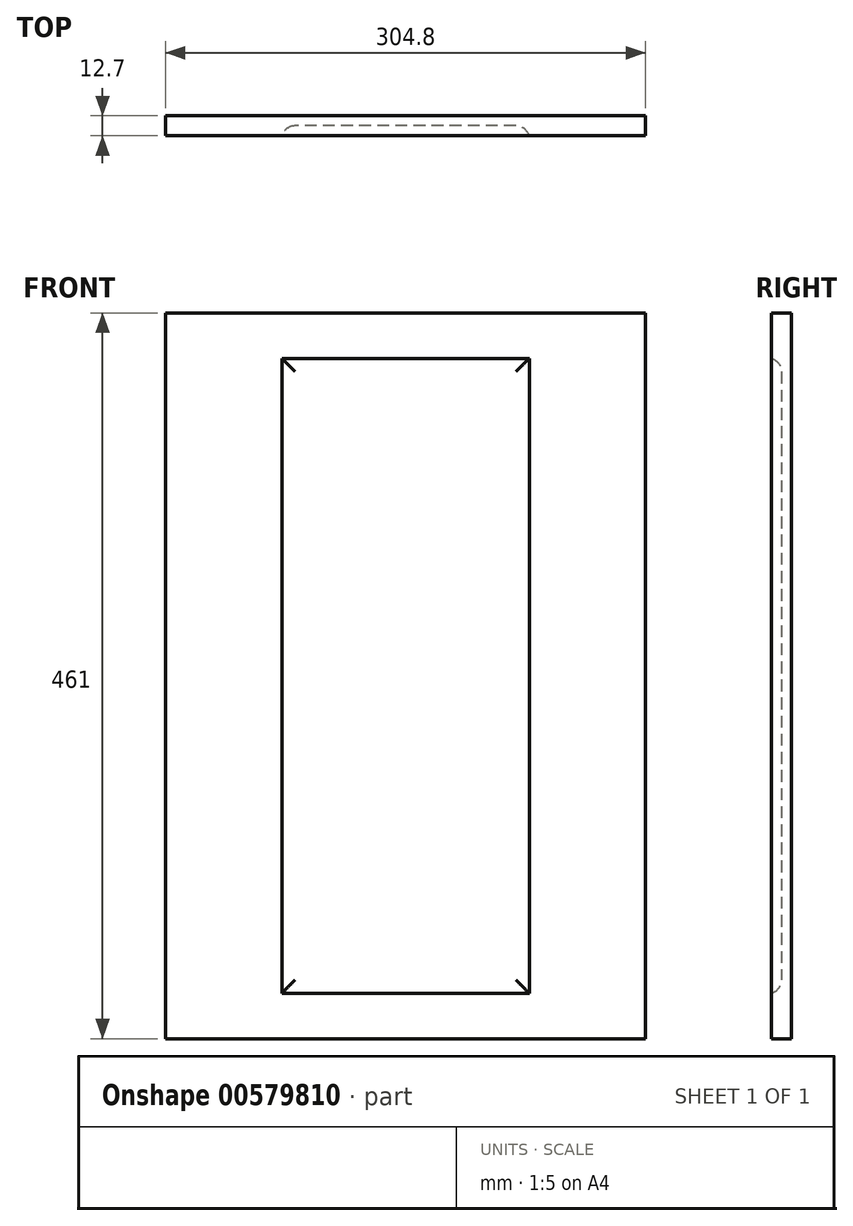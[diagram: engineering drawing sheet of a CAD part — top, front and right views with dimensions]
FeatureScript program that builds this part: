
annotation { "Feature Type Name" : "Feature", "Feature Type Description" : "" }
export const myFeature = defineFeature(function(context is Context, id is Id, definition is map)
    precondition{}
    {
        {
            var Q0;
            Q0=qCreatedBy(makeId("Front.planeOp"),FACE);
            var sketch = newSketch(context, id + "F0", { "sketchPlane" : qUnion([Q0])});
            skLineSegment(sketch, "E0.bottom", {"start": v(152.4, 230.5) * mm, "end": v(-152.4, 230.5) * mm});
            skLineSegment(sketch, "E0.top", {"start": v(152.4, -230.5) * mm, "end": v(-152.4, -230.5) * mm});
            skLineSegment(sketch, "E0.left", {"start": v(152.4, 230.5) * mm, "end": v(152.4, -230.5) * mm});
            skLineSegment(sketch, "E0.right", {"start": v(-152.4, 230.5) * mm, "end": v(-152.4, -230.5) * mm});
            skPoint(sketch, "E0.middle", {"position": v(0, 0) * mm});
            skSolve(sketch);
        }
        {
            var Q0;
            Q0=makeQuery(id+"F0.imprint","IMPRINT",FACE,{"disambiguationData":[TD([[makeQuery(id+"F0.imprint","IMPRINT",EDGE,{"derivedFrom":sQuery(id+"F0.wireOp",EDGE,"E0.bottom")}),1.0]])]});
            extrude(context, id + "F1", {"entities" : qUnion([Q0]), "depth" : 12.7 * mm, "offsetDistance" : 25.4 * mm});
        }
        {
            var Q0;
            Q0=makeQuery(id+"F1.opExtrude","CAP_FACE",FACE,{"disambiguationData":[OSD([sQuery(id+"F0.wireOp",EDGE,"E0.bottom"),sQuery(id+"F0.wireOp",EDGE,"E0.top"),sQuery(id+"F0.wireOp",EDGE,"E0.left"),sQuery(id+"F0.wireOp",EDGE,"E0.right")])],"isStart":false});
            var sketch = newSketch(context, id + "F2", { "sketchPlane" : qUnion([Q0])});
            skLineSegment(sketch, "E1.bottom", {"start": v(78.58, 201.62) * mm, "end": v(-78.58, 201.62) * mm});
            skLineSegment(sketch, "E1.top", {"start": v(78.58, -201.62) * mm, "end": v(-78.58, -201.62) * mm});
            skLineSegment(sketch, "E1.left", {"start": v(78.58, 201.62) * mm, "end": v(78.58, -201.62) * mm});
            skLineSegment(sketch, "E1.right", {"start": v(-78.58, 201.62) * mm, "end": v(-78.58, -201.62) * mm});
            skPoint(sketch, "E1.middle", {"position": v(0, 0) * mm});
            skSolve(sketch);
        }
        {
            var Q0;
            Q0=qSketchRegion(id+"F2",true);
            extrude(context, id + "F3", {"entities" : qUnion([Q0]), "operationType" : NewBodyOperationType.REMOVE, "oppositeDirection" : true, "depth" : 6.35 * mm, "offsetDistance" : 25.4 * mm});
        }
        {
            var Q0;
            Q0=makeQuery(id+"F3.boolean.opBoolean","COPY",FACE,{"derivedFrom":makeQuery(id+"F3.opExtrude","CAP_FACE",FACE,{"disambiguationData":[OSD([sQuery(id+"F2.wireOp",EDGE,"E1.bottom"),sQuery(id+"F2.wireOp",EDGE,"E1.top"),sQuery(id+"F2.wireOp",EDGE,"E1.left"),sQuery(id+"F2.wireOp",EDGE,"E1.right")])],"isStart":false})});
            fillet(context, id + "F4", {"entities" : qUnion([Q0]), "radius" : 8.9 * mm, "tangentPropagation" : true, "allowEdgeOverflow" : false});
        }
    });
